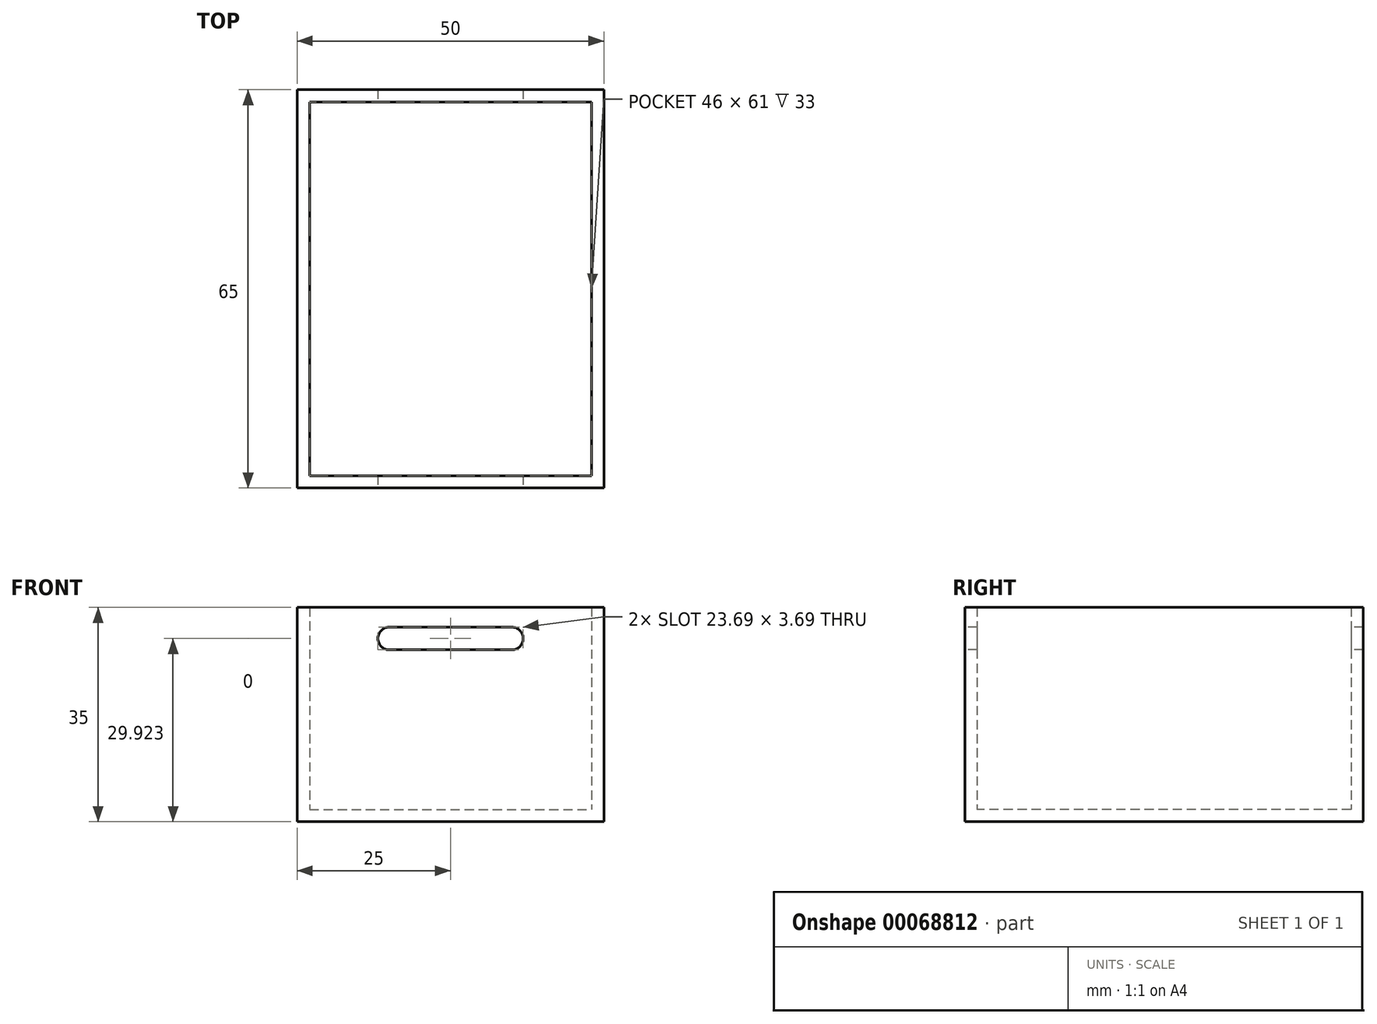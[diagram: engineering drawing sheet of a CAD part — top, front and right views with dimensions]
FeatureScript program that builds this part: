
annotation { "Feature Type Name" : "Feature", "Feature Type Description" : "" }
export const myFeature = defineFeature(function(context is Context, id is Id, definition is map)
    precondition{}
    {
        {
            var Q0;
            Q0=qCreatedBy(makeId("Top.planeOp"),FACE);
            var sketch = newSketch(context, id + "F0", { "sketchPlane" : qUnion([Q0])});
            skLineSegment(sketch, "E0.bottom", {"start": v(0, 0) * mm, "end": v(50, 0) * mm});
            skLineSegment(sketch, "E0.top", {"start": v(0, -65) * mm, "end": v(50, -65) * mm});
            skLineSegment(sketch, "E0.left", {"start": v(0, 0) * mm, "end": v(0, -65) * mm});
            skLineSegment(sketch, "E0.right", {"start": v(50, 0) * mm, "end": v(50, -65) * mm});
            skSolve(sketch);
        }
        {
            var Q0;
            Q0 = qSketchRegion(id + "F0", true);
            extrude(context, id + "F1", {"entities" : qUnion([Q0]), "depth" : 35 * mm});
        }
        {
            var Q0;
            Q0=makeQuery(id+"F1.opExtrude","CAP_FACE",FACE,{"disambiguationData":[OSD([sQuery(id+"F0.wireOp",EDGE,"E0.bottom"),sQuery(id+"F0.wireOp",EDGE,"E0.top"),sQuery(id+"F0.wireOp",EDGE,"E0.left"),sQuery(id+"F0.wireOp",EDGE,"E0.right")])],"isStart":false});
            shell(context, id + "F2", {"entities" : qUnion([Q0]), "thickness" : 2 * mm});
        }
        {
            var Q0;
            Q0=makeQuery(id+"F1.opExtrude","SWEPT_FACE",FACE,{"disambiguationData":[OSD([sQuery(id+"F0.wireOp",EDGE,"E0.top")])]});
            var sketch = newSketch(context, id + "F3", { "sketchPlane" : qUnion([Q0])});
            skArc(sketch, "E1", {"start": v(15, 31.77) * mm, "mid": v(13.15, 29.92) * mm, "end": v(15, 28.08) * mm});
            skArc(sketch, "E2", {"start": v(35, 28.08) * mm, "mid": v(36.85, 29.92) * mm, "end": v(35, 31.77) * mm});
            skLineSegment(sketch, "E3", {"start": v(15, 31.77) * mm, "end": v(35, 31.77) * mm});
            skLineSegment(sketch, "E4", {"start": v(15, 28.08) * mm, "end": v(35, 28.08) * mm});
            skLineSegment(sketch, "E5", {"start": v(25, 35) * mm, "end": v(25, 0) * mm, "construction": true});
            skLineSegment(sketch, "E6", {"start": v(15, 29.92) * mm, "end": v(35, 29.92) * mm, "construction": true});
            skSolve(sketch);
        }
        {
            var Q0;
            Q0=makeQuery(id+"F3.imprint","IMPRINT",FACE,{"disambiguationData":[TD([[makeQuery(id+"F3.imprint","IMPRINT",EDGE,{"derivedFrom":sQuery(id+"F3.wireOp",EDGE,"E1")}),1.0]])]});
            extrude(context, id + "F4", {"entities" : qUnion([Q0]), "operationType" : NewBodyOperationType.REMOVE, "endBound" : BoundingType.SYMMETRIC, "oppositeDirection" : true, "depth" : 200 * mm});
        }
    });
